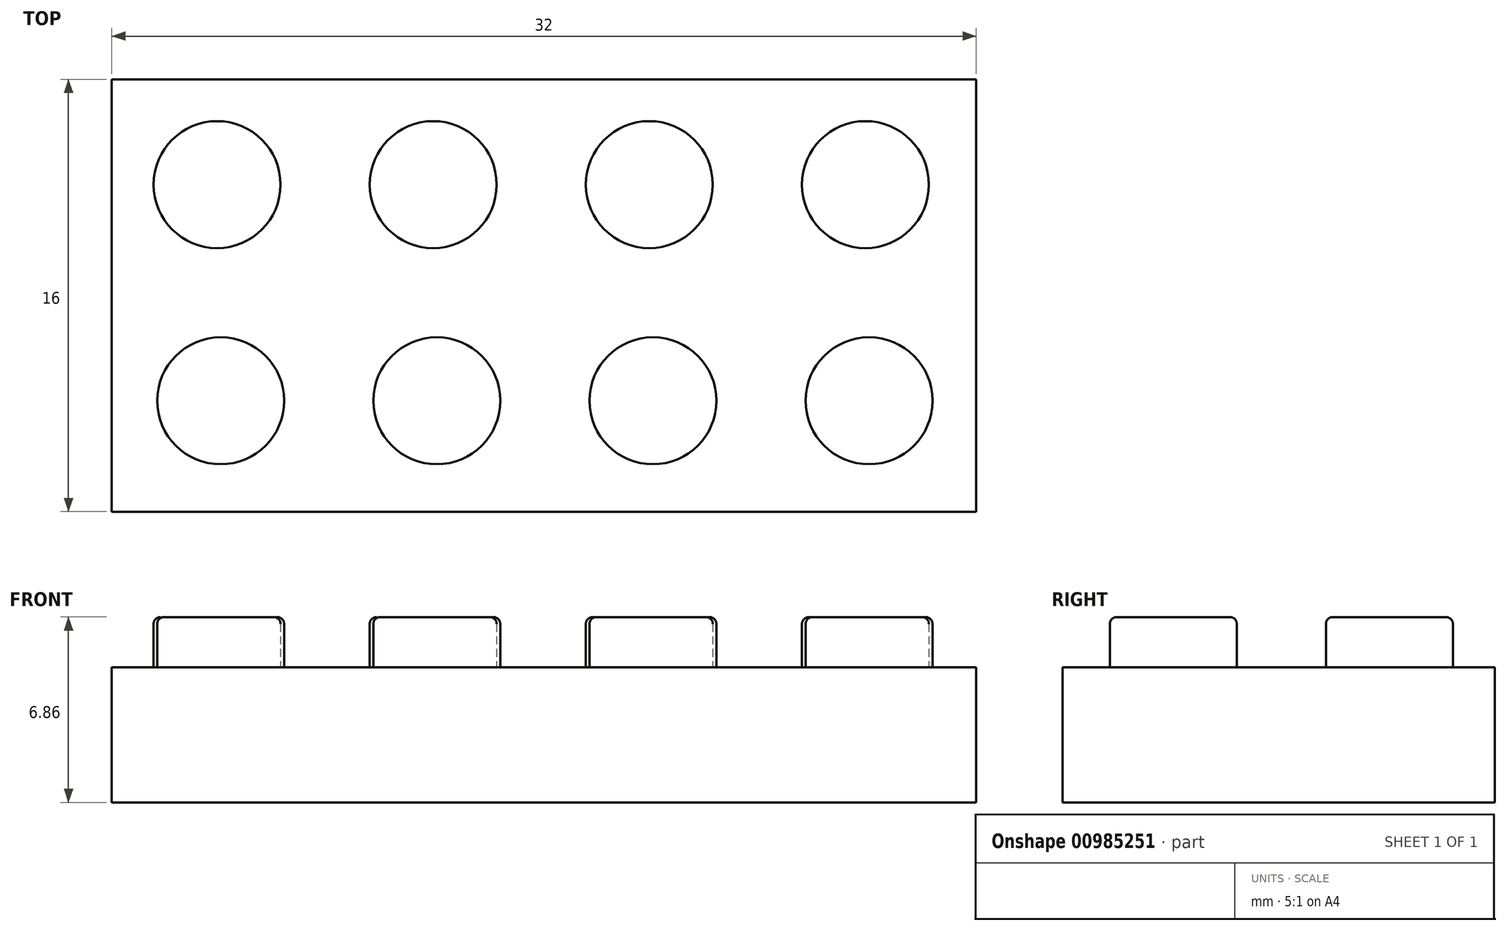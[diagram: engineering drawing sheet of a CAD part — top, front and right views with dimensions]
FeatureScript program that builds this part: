
annotation { "Feature Type Name" : "Feature", "Feature Type Description" : "" }
export const myFeature = defineFeature(function(context is Context, id is Id, definition is map)
    precondition{}
    {
        {
            var Q0;
            Q0=qCreatedBy(makeId("Top.planeOp"),FACE);
            var sketch = newSketch(context, id + "F0", { "sketchPlane" : qUnion([Q0])});
            skLineSegment(sketch, "E0.bottom", {"start": v(0, 0) * mm, "end": v(32, 0) * mm});
            skLineSegment(sketch, "E0.top", {"start": v(0, -16) * mm, "end": v(32, -16) * mm});
            skLineSegment(sketch, "E0.left", {"start": v(0, 0) * mm, "end": v(0, -16) * mm});
            skLineSegment(sketch, "E0.right", {"start": v(32, 0) * mm, "end": v(32, -16) * mm});
            skSolve(sketch);
        }
        {
            var Q0;
            Q0=makeQuery(id+"F0.imprint","IMPRINT",FACE,{"disambiguationData":[TD([[makeQuery(id+"F0.imprint","IMPRINT",EDGE,{"derivedFrom":sQuery(id+"F0.wireOp",EDGE,"E0.bottom")}),-1.0]])]});
            extrude(context, id + "F1", {"entities" : qUnion([Q0]), "depth" : 5 * mm, "offsetDistance" : 25.4 * mm});
        }
        {
            var Q0;
            Q0=makeQuery(id+"F1.opExtrude","CAP_FACE",FACE,{"disambiguationData":[OSD([sQuery(id+"F0.wireOp",EDGE,"E0.bottom"),sQuery(id+"F0.wireOp",EDGE,"E0.top"),sQuery(id+"F0.wireOp",EDGE,"E0.left"),sQuery(id+"F0.wireOp",EDGE,"E0.right")])],"isStart":false});
            var sketch = newSketch(context, id + "F2", { "sketchPlane" : qUnion([Q0])});
            skCircle(sketch, "E1", {"center": v(3.9, -3.9) * mm, "radius": 2.35 * mm});
            skCircle(sketch, "E2.1.0.0", {"center": v(11.9, -3.9) * mm, "radius": 2.35 * mm});
            skCircle(sketch, "E2.2.0.0", {"center": v(19.9, -3.9) * mm, "radius": 2.35 * mm});
            skCircle(sketch, "E2.3.0.0", {"center": v(27.9, -3.9) * mm, "radius": 2.35 * mm});
            skLineSegment(sketch, "E2.direction1", {"start": v(3.9, -3.9) * mm, "end": v(11.9, -3.9) * mm, "construction": true});
            skCircle(sketch, "E3.1.0.0", {"center": v(4.03, -11.9) * mm, "radius": 2.35 * mm});
            skCircle(sketch, "E3.1.0.1", {"center": v(12.03, -11.9) * mm, "radius": 2.35 * mm});
            skCircle(sketch, "E3.1.0.2", {"center": v(20.04, -11.9) * mm, "radius": 2.35 * mm});
            skCircle(sketch, "E3.1.0.3", {"center": v(28.04, -11.9) * mm, "radius": 2.35 * mm});
            skLineSegment(sketch, "E3.direction1", {"start": v(3.9, -3.9) * mm, "end": v(4.03, -11.9) * mm, "construction": true});
            skSolve(sketch);
        }
        {
            var Q0;
            Q0 = qSketchRegion(id + "F2", true);
            extrude(context, id + "F3", {"entities" : qUnion([Q0]), "operationType" : NewBodyOperationType.ADD, "depth" : 1.85 * mm, "offsetDistance" : 25.4 * mm});
        }
        {
            var Q0;
            Q0=makeQuery(id+"F3.opExtrude","CAP_EDGE",EDGE,{"disambiguationData":[OSD([sQuery(id+"F2.wireOp",EDGE,"E1")])],"isStart":false});
            var Q1;
            Q1=makeQuery(id+"F3.opExtrude","CAP_EDGE",EDGE,{"disambiguationData":[OSD([sQuery(id+"F2.wireOp",EDGE,"E2.1.0.0")])],"isStart":false});
            var Q2;
            Q2=makeQuery(id+"F3.opExtrude","CAP_EDGE",EDGE,{"disambiguationData":[OSD([sQuery(id+"F2.wireOp",EDGE,"E2.2.0.0")])],"isStart":false});
            var Q3;
            Q3=makeQuery(id+"F3.opExtrude","CAP_EDGE",EDGE,{"disambiguationData":[OSD([sQuery(id+"F2.wireOp",EDGE,"E2.3.0.0")])],"isStart":false});
            var Q4;
            Q4=makeQuery(id+"F3.opExtrude","CAP_EDGE",EDGE,{"disambiguationData":[OSD([sQuery(id+"F2.wireOp",EDGE,"E3.1.0.3")])],"isStart":false});
            var Q5;
            Q5=makeQuery(id+"F3.opExtrude","CAP_EDGE",EDGE,{"disambiguationData":[OSD([sQuery(id+"F2.wireOp",EDGE,"E3.1.0.2")])],"isStart":false});
            var Q6;
            Q6=makeQuery(id+"F3.opExtrude","CAP_EDGE",EDGE,{"disambiguationData":[OSD([sQuery(id+"F2.wireOp",EDGE,"E3.1.0.1")])],"isStart":false});
            var Q7;
            Q7=makeQuery(id+"F3.opExtrude","CAP_EDGE",EDGE,{"disambiguationData":[OSD([sQuery(id+"F2.wireOp",EDGE,"E3.1.0.0")])],"isStart":false});
            fillet(context, id + "F4", {"entities" : qUnion([Q0, Q1, Q2, Q3, Q4, Q5, Q6, Q7]), "radius" : 0.25 * mm, "tangentPropagation" : true, "allowEdgeOverflow" : false});
        }
    });
